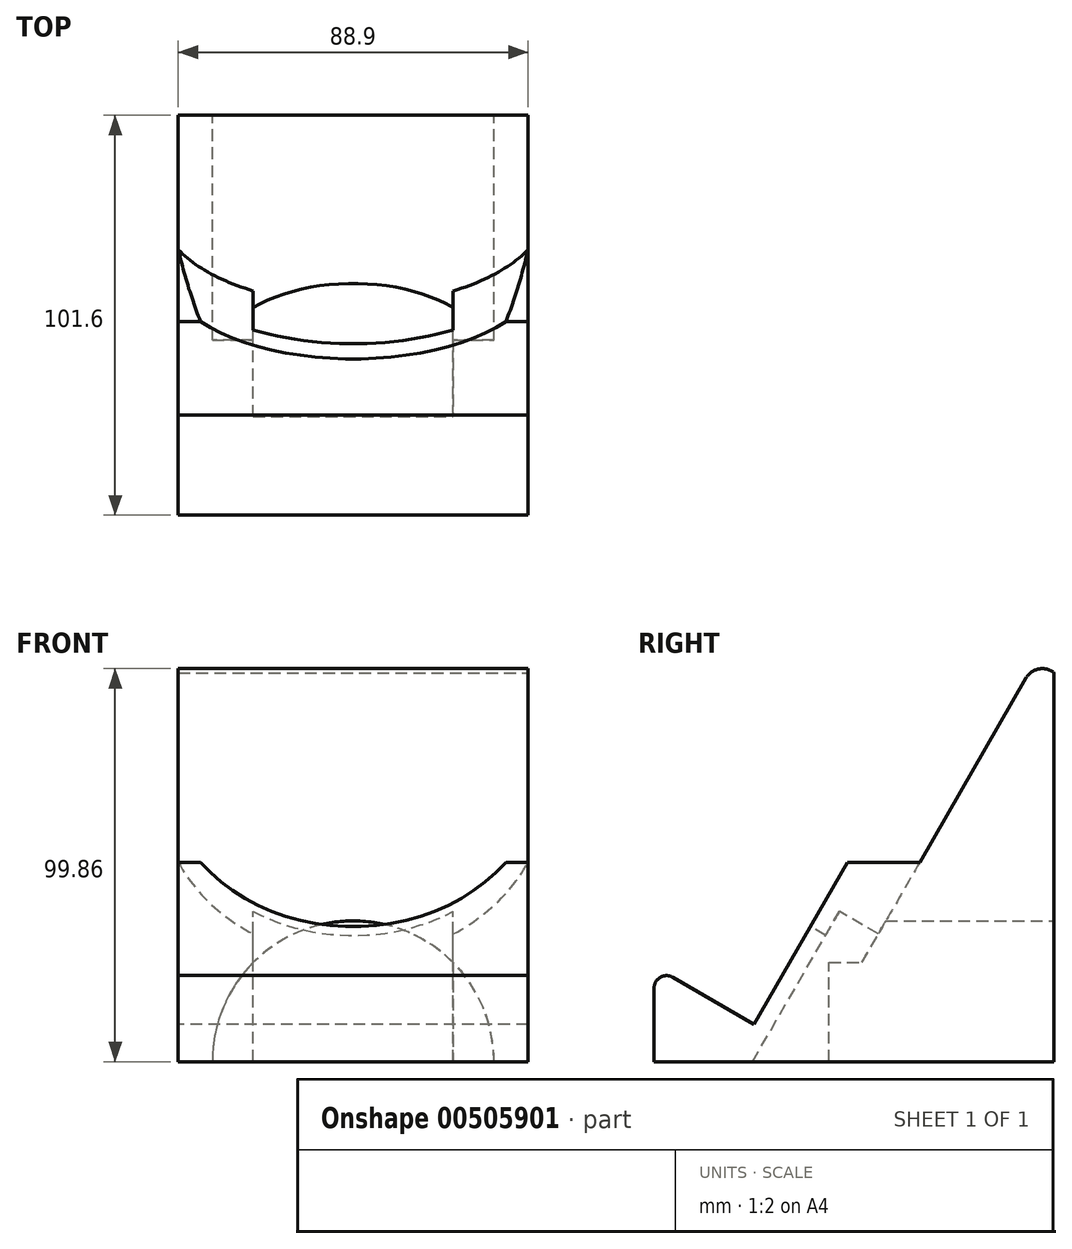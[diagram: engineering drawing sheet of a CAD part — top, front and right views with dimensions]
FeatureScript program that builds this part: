
annotation { "Feature Type Name" : "Feature", "Feature Type Description" : "" }
export const myFeature = defineFeature(function(context is Context, id is Id, definition is map)
    precondition{}
    {
        {
            var Q0;
            Q0=qCreatedBy(makeId("Right.planeOp"),FACE);
            var sketch = newSketch(context, id + "F0", { "sketchPlane" : qUnion([Q0])});
            skLineSegment(sketch, "E0", {"start": v(0, 0) * mm, "end": v(101.6, 0) * mm});
            skLineSegment(sketch, "E1", {"start": v(101.6, 0) * mm, "end": v(101.6, 101.6) * mm});
            skLineSegment(sketch, "E2", {"start": v(101.6, 101.6) * mm, "end": v(78.56, 101.6) * mm});
            skLineSegment(sketch, "E3", {"start": v(78.56, 101.6) * mm, "end": v(25.4, 9.52) * mm});
            skLineSegment(sketch, "E4", {"start": v(25.4, 9.53) * mm, "end": v(0, 9.53) * mm});
            skLineSegment(sketch, "E5", {"start": v(0, 9.52) * mm, "end": v(0, 0) * mm});
            skSolve(sketch);
        }
        {
            var Q0;
            Q0 = qSketchRegion(id + "F0", true);
            extrude(context, id + "F1", {"entities" : qUnion([Q0]), "depth" : 88.9 * mm, "offsetDistance" : 25.4 * mm});
        }
        {
            var Q0;
            Q0=makeQuery(id+"F1.opExtrude","SWEPT_FACE",FACE,{"disambiguationData":[OSD([sQuery(id+"F0.wireOp",EDGE,"E3")])]});
            var sketch = newSketch(context, id + "F2", { "sketchPlane" : qUnion([Q0])});
            skPoint(sketch, "E6", {"position": v(44.45, 98.74) * mm});
            skArc(sketch, "E7", {"start": v(-3.8, 108.46) * mm, "mid": v(44.45, 49.52) * mm, "end": v(92.7, 108.46) * mm});
            skLineSegment(sketch, "E8", {"start": v(88.9, 127.27) * mm, "end": v(92.7, 108.46) * mm});
            skLineSegment(sketch, "E9", {"start": v(0, 127.27) * mm, "end": v(-3.8, 108.46) * mm});
            skPoint(sketch, "E10.orphan", {"position": v(94.65, 98.74) * mm});
            skPoint(sketch, "E11.orphan", {"position": v(-5.75, 98.74) * mm});
            skLineSegment(sketch, "E12", {"start": v(0, 127.27) * mm, "end": v(0, 140.52) * mm});
            skLineSegment(sketch, "E13", {"start": v(0, 140.52) * mm, "end": v(88.9, 140.52) * mm});
            skLineSegment(sketch, "E14", {"start": v(88.9, 140.52) * mm, "end": v(88.9, 127.27) * mm});
            skSolve(sketch);
        }
        {
            var Q0;
            Q0 = qSketchRegion(id + "F2", true);
            extrude(context, id + "F3", {"entities" : qUnion([Q0]), "operationType" : NewBodyOperationType.REMOVE, "oppositeDirection" : true, "depth" : 15.88 * mm, "offsetDistance" : 25.4 * mm});
        }
        {
            var Q0;
            Q0=makeQuery(id+"F1.opExtrude","CAP_FACE",FACE,{"disambiguationData":[OSD([sQuery(id+"F0.wireOp",EDGE,"E0"),sQuery(id+"F0.wireOp",EDGE,"E1"),sQuery(id+"F0.wireOp",EDGE,"E2"),sQuery(id+"F0.wireOp",EDGE,"E3"),sQuery(id+"F0.wireOp",EDGE,"E4"),sQuery(id+"F0.wireOp",EDGE,"E5")])],"isStart":false});
            var sketch = newSketch(context, id + "F4", { "sketchPlane" : qUnion([Q0])});
            skLineSegment(sketch, "E15", {"start": v(96.9, 101.6) * mm, "end": v(110.13, 93.95) * mm});
            skLineSegment(sketch, "E16", {"start": v(110.13, 93.95) * mm, "end": v(117.44, 106.61) * mm});
            skLineSegment(sketch, "E17", {"start": v(117.44, 106.61) * mm, "end": v(103.98, 114.39) * mm});
            skLineSegment(sketch, "E18", {"start": v(103.98, 114.39) * mm, "end": v(96.9, 101.6) * mm});
            skSolve(sketch);
        }
        {
            var Q0;
            Q0 = qSketchRegion(id + "F4", true);
            extrude(context, id + "F5", {"entities" : qUnion([Q0]), "operationType" : NewBodyOperationType.REMOVE, "endBound" : BoundingType.THROUGH_ALL, "oppositeDirection" : true, "depth" : 25.4 * mm, "offsetDistance" : 25.4 * mm});
        }
        {
            var Q0;
            Q0=makeQuery(id+"F5.boolean.opBoolean","COPY",FACE,{"derivedFrom":makeQuery(id+"F5.opExtrude","SWEPT_FACE",FACE,{"disambiguationData":[OSD([sQuery(id+"F4.wireOp",EDGE,"E15")])]})});
            var sketch = newSketch(context, id + "F6", { "sketchPlane" : qUnion([Q0])});
            skLineSegment(sketch, "E19", {"start": v(19.05, 21.68) * mm, "end": v(19.05, 33.1) * mm});
            skLineSegment(sketch, "E20", {"start": v(19.05, 33.1) * mm, "end": v(69.85, 33.1) * mm});
            skLineSegment(sketch, "E21", {"start": v(69.85, 33.1) * mm, "end": v(69.85, 21.68) * mm});
            skLineSegment(sketch, "E22", {"start": v(19.05, 21.68) * mm, "end": v(69.85, 21.68) * mm});
            skSolve(sketch);
        }
        {
            var Q0;
            Q0 = qSketchRegion(id + "F6", true);
            extrude(context, id + "F7", {"entities" : qUnion([Q0]), "operationType" : NewBodyOperationType.REMOVE, "endBound" : BoundingType.THROUGH_ALL, "oppositeDirection" : true, "depth" : 25.4 * mm, "offsetDistance" : 25.4 * mm});
        }
        {
            var Q0;
            Q0=makeQuery(id+"F1.opExtrude","SWEPT_FACE",FACE,{"disambiguationData":[OSD([sQuery(id+"F0.wireOp",EDGE,"E1")])]});
            var sketch = newSketch(context, id + "F8", { "sketchPlane" : qUnion([Q0])});
            skCircle(sketch, "E23", {"center": v(-44.45, 0) * mm, "radius": 35.77 * mm});
            skSolve(sketch);
        }
        {
            var Q0;
            Q0 = qSketchRegion(id + "F8", true);
            extrude(context, id + "F9", {"entities" : qUnion([Q0]), "operationType" : NewBodyOperationType.REMOVE, "oppositeDirection" : true, "depth" : 57.15 * mm, "offsetDistance" : 25.4 * mm});
        }
        {
            var Q0;
            Q0=makeQuery(id+"F1.opExtrude","SWEPT_FACE",FACE,{"disambiguationData":[OSD([sQuery(id+"F0.wireOp",EDGE,"E0")])]});
            var sketch = newSketch(context, id + "F10", { "sketchPlane" : qUnion([Q0])});
            skLineSegment(sketch, "E24", {"start": v(19.05, -38.23) * mm, "end": v(19.05, -44.45) * mm});
            skLineSegment(sketch, "E25", {"start": v(19.05, -38.23) * mm, "end": v(69.85, -38.23) * mm});
            skLineSegment(sketch, "E26", {"start": v(69.85, -38.23) * mm, "end": v(69.85, -44.45) * mm});
            skLineSegment(sketch, "E27", {"start": v(69.85, -44.45) * mm, "end": v(19.05, -44.45) * mm});
            skSolve(sketch);
        }
        {
            var Q0;
            Q0 = qSketchRegion(id + "F10", true);
            extrude(context, id + "F11", {"entities" : qUnion([Q0]), "operationType" : NewBodyOperationType.REMOVE, "endBound" : BoundingType.UP_TO_NEXT, "oppositeDirection" : true, "depth" : 25.4 * mm, "offsetDistance" : 25.4 * mm});
        }
        {
            var Q0;
            Q0=makeQuery(id+"F1.opExtrude","CAP_FACE",FACE,{"disambiguationData":[OSD([sQuery(id+"F0.wireOp",EDGE,"E0"),sQuery(id+"F0.wireOp",EDGE,"E1"),sQuery(id+"F0.wireOp",EDGE,"E2"),sQuery(id+"F0.wireOp",EDGE,"E3"),sQuery(id+"F0.wireOp",EDGE,"E4"),sQuery(id+"F0.wireOp",EDGE,"E5")])],"isStart":false});
            var sketch = newSketch(context, id + "F12", { "sketchPlane" : qUnion([Q0])});
            skLineSegment(sketch, "E28", {"start": v(25.4, 9.52) * mm, "end": v(4.76, 21.44) * mm});
            skLineSegment(sketch, "E29", {"start": v(0, 18.7) * mm, "end": v(0, 9.53) * mm});
            skLineSegment(sketch, "E30", {"start": v(0, 9.53) * mm, "end": v(25.4, 9.52) * mm});
            skPoint(sketch, "E31.visualSharp", {"position": v(0, 24.19) * mm});
            skArc(sketch, "E31.filletArc", {"start": v(4.76, 21.44) * mm, "mid": v(1.59, 21.44) * mm, "end": v(0, 18.7) * mm});
            skSolve(sketch);
        }
        {
            var Q0;
            Q0 = qSketchRegion(id + "F12", true);
            extrude(context, id + "F13", {"entities" : qUnion([Q0]), "operationType" : NewBodyOperationType.ADD, "oppositeDirection" : true, "depth" : 88.9 * mm, "offsetDistance" : 25.4 * mm});
        }
        {
            var Q0;
            Q0=makeQuery(id+"F13.boolean.opBoolean","MERGE",FACE,{"derivedFrom":[makeQuery(id+"F1.opExtrude","CAP_FACE",FACE,{"disambiguationData":[OSD([sQuery(id+"F0.wireOp",EDGE,"E0"),sQuery(id+"F0.wireOp",EDGE,"E1"),sQuery(id+"F0.wireOp",EDGE,"E2"),sQuery(id+"F0.wireOp",EDGE,"E3"),sQuery(id+"F0.wireOp",EDGE,"E4"),sQuery(id+"F0.wireOp",EDGE,"E5")])],"isStart":false}),makeQuery(id+"F13.opExtrude","CAP_FACE",FACE,{"disambiguationData":[OSD([sQuery(id+"F12.wireOp",EDGE,"E28"),sQuery(id+"F12.wireOp",EDGE,"E29"),sQuery(id+"F12.wireOp",EDGE,"E30"),sQuery(id+"F12.wireOp",EDGE,"E31.filletArc")])],"isStart":true})]});
            var sketch = newSketch(context, id + "F14", { "sketchPlane" : qUnion([Q0])});
            skLineSegment(sketch, "E32", {"start": v(67.48, 50.66) * mm, "end": v(49.15, 50.66) * mm});
            skLineSegment(sketch, "E33", {"start": v(49.15, 50.66) * mm, "end": v(53.73, 58.6) * mm});
            skLineSegment(sketch, "E34", {"start": v(53.73, 58.6) * mm, "end": v(67.48, 50.66) * mm});
            skSolve(sketch);
        }
        {
            var Q0;
            Q0 = qSketchRegion(id + "F14", true);
            extrude(context, id + "F15", {"entities" : qUnion([Q0]), "operationType" : NewBodyOperationType.REMOVE, "endBound" : BoundingType.THROUGH_ALL, "oppositeDirection" : true, "depth" : 25.4 * mm, "offsetDistance" : 25.4 * mm});
        }
        {
            var Q0;
            Q0=makeQuery(id+"F13.boolean.opBoolean","MERGE",FACE,{"derivedFrom":[makeQuery(id+"F1.opExtrude","CAP_FACE",FACE,{"disambiguationData":[OSD([sQuery(id+"F0.wireOp",EDGE,"E0"),sQuery(id+"F0.wireOp",EDGE,"E1"),sQuery(id+"F0.wireOp",EDGE,"E2"),sQuery(id+"F0.wireOp",EDGE,"E3"),sQuery(id+"F0.wireOp",EDGE,"E4"),sQuery(id+"F0.wireOp",EDGE,"E5")])],"isStart":false}),makeQuery(id+"F13.opExtrude","CAP_FACE",FACE,{"disambiguationData":[OSD([sQuery(id+"F12.wireOp",EDGE,"E28"),sQuery(id+"F12.wireOp",EDGE,"E29"),sQuery(id+"F12.wireOp",EDGE,"E30"),sQuery(id+"F12.wireOp",EDGE,"E31.filletArc")])],"isStart":true})]});
            var sketch = newSketch(context, id + "F16", { "sketchPlane" : qUnion([Q0])});
            skArc(sketch, "E35", {"start": v(101.6, 98.82) * mm, "mid": v(97.75, 99.77) * mm, "end": v(94.5, 97.48) * mm});
            skLineSegment(sketch, "E36", {"start": v(96.9, 101.6) * mm, "end": v(94.5, 97.48) * mm});
            skLineSegment(sketch, "E37", {"start": v(96.9, 101.6) * mm, "end": v(101.6, 98.88) * mm});
            skLineSegment(sketch, "E38", {"start": v(101.6, 98.88) * mm, "end": v(101.6, 98.82) * mm});
            skSolve(sketch);
        }
        {
            var Q0;
            Q0 = qSketchRegion(id + "F16", true);
            extrude(context, id + "F17", {"entities" : qUnion([Q0]), "operationType" : NewBodyOperationType.REMOVE, "endBound" : BoundingType.THROUGH_ALL, "oppositeDirection" : true, "depth" : 25.4 * mm, "offsetDistance" : 25.4 * mm});
        }
    });
